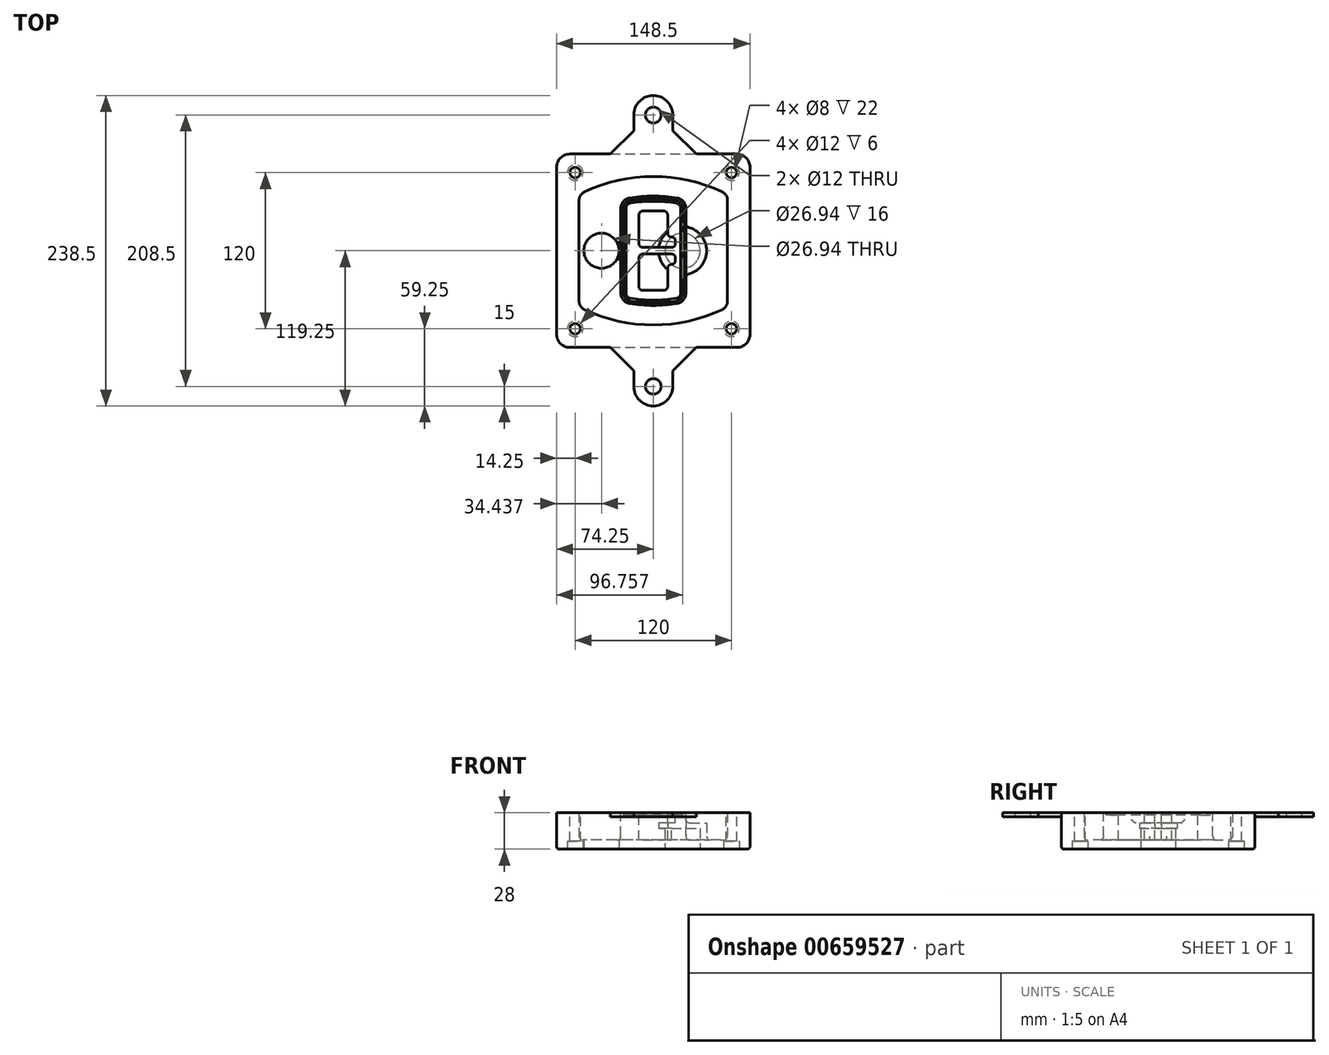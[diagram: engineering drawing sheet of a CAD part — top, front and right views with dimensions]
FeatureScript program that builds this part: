
annotation { "Feature Type Name" : "Feature", "Feature Type Description" : "" }
export const myFeature = defineFeature(function(context is Context, id is Id, definition is map)
    precondition{}
    {
        {
            var Q0;
            Q0=qCreatedBy(makeId("Top.planeOp"),FACE);
            var sketch = newSketch(context, id + "F0", { "sketchPlane" : qUnion([Q0])});
            skPoint(sketch, "E0.rect.middle", {"position": v(0, 0) * mm});
            skLineSegment(sketch, "E1.bottom", {"start": v(-64.25, -74.25) * mm, "end": v(64.25, -74.25) * mm});
            skLineSegment(sketch, "E1.top", {"start": v(-64.25, 74.25) * mm, "end": v(64.25, 74.25) * mm});
            skLineSegment(sketch, "E1.left", {"start": v(-74.25, -64.25) * mm, "end": v(-74.25, 64.25) * mm});
            skLineSegment(sketch, "E1.right", {"start": v(74.25, -64.25) * mm, "end": v(74.25, 64.25) * mm});
            skLineSegment(sketch, "E2", {"start": v(-74.25, 74.25) * mm, "end": v(74.25, -74.25) * mm, "construction": true});
            skLineSegment(sketch, "E3", {"start": v(74.25, 74.25) * mm, "end": v(-74.25, -74.25) * mm, "construction": true});
            skCircle(sketch, "E4", {"center": v(-60, 60) * mm, "radius": 4 * mm});
            skCircle(sketch, "E5", {"center": v(60, 60) * mm, "radius": 4 * mm});
            skCircle(sketch, "E6", {"center": v(60, -60) * mm, "radius": 4 * mm});
            skCircle(sketch, "E7", {"center": v(-60, -60) * mm, "radius": 4 * mm});
            skLineSegment(sketch, "E8", {"start": v(-60, 60) * mm, "end": v(60, 60) * mm, "construction": true});
            skLineSegment(sketch, "E9", {"start": v(60, 60) * mm, "end": v(60, -60) * mm, "construction": true});
            skLineSegment(sketch, "E10", {"start": v(60, -60) * mm, "end": v(-60, -60) * mm, "construction": true});
            skLineSegment(sketch, "E11", {"start": v(-60, -60) * mm, "end": v(-60, 60) * mm, "construction": true});
            skLineSegment(sketch, "E12", {"start": v(-60, 38.83) * mm, "end": v(-60, -38.83) * mm});
            skLineSegment(sketch, "E13", {"start": v(60, 38.83) * mm, "end": v(60, -38.83) * mm});
            skArc(sketch, "E14", {"start": v(54.26, 47.88) * mm, "mid": v(0, 60) * mm, "end": v(-54.26, 47.88) * mm});
            skArc(sketch, "E15", {"start": v(-54.26, -47.88) * mm, "mid": v(0, -60) * mm, "end": v(54.26, -47.88) * mm});
            skLineSegment(sketch, "E16", {"start": v(-60, 0) * mm, "end": v(60, 0) * mm, "construction": true});
            skPoint(sketch, "E17.visualSharp", {"position": v(-60, -45) * mm});
            skArc(sketch, "E17.filletArc", {"start": v(-60, -38.83) * mm, "mid": v(-58.44, -44.2) * mm, "end": v(-54.26, -47.88) * mm});
            skPoint(sketch, "E18.visualSharp", {"position": v(-60, 45) * mm});
            skArc(sketch, "E18.filletArc", {"start": v(-54.26, 47.88) * mm, "mid": v(-58.44, 44.2) * mm, "end": v(-60, 38.83) * mm});
            skPoint(sketch, "E19.visualSharp", {"position": v(60, 45) * mm});
            skArc(sketch, "E19.filletArc", {"start": v(60, 38.83) * mm, "mid": v(58.44, 44.2) * mm, "end": v(54.26, 47.88) * mm});
            skPoint(sketch, "E20.visualSharp", {"position": v(60, -45) * mm});
            skArc(sketch, "E20.filletArc", {"start": v(54.26, -47.88) * mm, "mid": v(58.44, -44.2) * mm, "end": v(60, -38.83) * mm});
            skPoint(sketch, "E21.visualSharp", {"position": v(-74.25, 74.25) * mm});
            skArc(sketch, "E21.filletArc", {"start": v(-64.25, 74.25) * mm, "mid": v(-71.32, 71.32) * mm, "end": v(-74.25, 64.25) * mm});
            skPoint(sketch, "E22.visualSharp", {"position": v(74.25, 74.25) * mm});
            skArc(sketch, "E22.filletArc", {"start": v(74.25, 64.25) * mm, "mid": v(71.32, 71.32) * mm, "end": v(64.25, 74.25) * mm});
            skPoint(sketch, "E23.visualSharp", {"position": v(74.25, -74.25) * mm});
            skArc(sketch, "E23.filletArc", {"start": v(64.25, -74.25) * mm, "mid": v(71.32, -71.32) * mm, "end": v(74.25, -64.25) * mm});
            skPoint(sketch, "E24.visualSharp", {"position": v(-74.25, -74.25) * mm});
            skArc(sketch, "E24.filletArc", {"start": v(-74.25, -64.25) * mm, "mid": v(-71.32, -71.32) * mm, "end": v(-64.25, -74.25) * mm});
            skArc(sketch, "E25.0", {"start": v(57, 38.83) * mm, "mid": v(55.9, 42.58) * mm, "end": v(52.98, 45.17) * mm});
            skLineSegment(sketch, "E25.1", {"start": v(57, 38.83) * mm, "end": v(57, -38.83) * mm});
            skArc(sketch, "E25.2", {"start": v(52.98, -45.17) * mm, "mid": v(55.9, -42.58) * mm, "end": v(57, -38.83) * mm});
            skArc(sketch, "E25.3", {"start": v(-52.98, -45.17) * mm, "mid": v(0, -57) * mm, "end": v(52.98, -45.17) * mm});
            skArc(sketch, "E25.4", {"start": v(-57, -38.83) * mm, "mid": v(-55.9, -42.58) * mm, "end": v(-52.98, -45.17) * mm});
            skArc(sketch, "E25.5", {"start": v(52.98, 45.17) * mm, "mid": v(0, 57) * mm, "end": v(-52.98, 45.17) * mm});
            skLineSegment(sketch, "E25.6", {"start": v(-57, 38.83) * mm, "end": v(-57, -38.83) * mm});
            skArc(sketch, "E25.7", {"start": v(-52.98, 45.17) * mm, "mid": v(-55.9, 42.58) * mm, "end": v(-57, 38.83) * mm});
            skArc(sketch, "E26.0", {"start": v(-55.96, 51.5) * mm, "mid": v(-61.82, 46.33) * mm, "end": v(-64, 38.83) * mm});
            skArc(sketch, "E26.1", {"start": v(55.96, 51.5) * mm, "mid": v(0, 64) * mm, "end": v(-55.96, 51.5) * mm});
            skArc(sketch, "E26.2", {"start": v(64, 38.83) * mm, "mid": v(61.82, 46.33) * mm, "end": v(55.96, 51.5) * mm});
            skLineSegment(sketch, "E26.3", {"start": v(64, 38.83) * mm, "end": v(64, -38.83) * mm});
            skArc(sketch, "E26.4", {"start": v(55.96, -51.5) * mm, "mid": v(61.82, -46.33) * mm, "end": v(64, -38.83) * mm});
            skLineSegment(sketch, "E26.5", {"start": v(-64, 38.83) * mm, "end": v(-64, -38.83) * mm});
            skArc(sketch, "E26.6", {"start": v(-55.96, -51.5) * mm, "mid": v(0, -64) * mm, "end": v(55.96, -51.5) * mm});
            skArc(sketch, "E26.7", {"start": v(-64, -38.83) * mm, "mid": v(-61.82, -46.33) * mm, "end": v(-55.96, -51.5) * mm});
            skSolve(sketch);
        }
        {
            var Q0;
            Q0=makeQuery(id+"F0.imprint","IMPRINT",FACE,{"disambiguationData":[TD([[makeQuery(id+"F0.imprint","IMPRINT",EDGE,{"derivedFrom":sQuery(id+"F0.wireOp",EDGE,"E1.bottom")}),1.0]])]});
            var Q1;
            Q1=makeQuery(id+"F0.imprint","IMPRINT",FACE,{"disambiguationData":[TD([[makeQuery(id+"F0.imprint","IMPRINT",EDGE,{"derivedFrom":sQuery(id+"F0.wireOp",EDGE,"E12")}),1.0]])]});
            var Q2;
            Q2=makeQuery(id+"F0.imprint","IMPRINT",FACE,{"disambiguationData":[TD([[makeQuery(id+"F0.imprint","IMPRINT",EDGE,{"derivedFrom":sQuery(id+"F0.wireOp",EDGE,"E25.0")}),1.0]])]});
            var Q3;
            Q3=makeQuery(id+"F0.imprint","IMPRINT",FACE,{"disambiguationData":[TD([[makeQuery(id+"F0.imprint","IMPRINT",EDGE,{"derivedFrom":sQuery(id+"F0.wireOp",EDGE,"E12")}),-1.0]])]});
            extrude(context, id + "F1", {"entities" : qUnion([Q0, Q1, Q2, Q3]), "oppositeDirection" : true, "depth" : 25 * mm});
        }
        {
            var Q0;
            Q0=makeQuery(id+"F0.imprint","IMPRINT",FACE,{"disambiguationData":[TD([[makeQuery(id+"F0.imprint","IMPRINT",EDGE,{"derivedFrom":sQuery(id+"F0.wireOp",EDGE,"E12")}),1.0]])]});
            extrude(context, id + "F2", {"entities" : qUnion([Q0]), "operationType" : NewBodyOperationType.ADD, "depth" : 3 * mm});
        }
        {
            var Q0;
            Q0=makeQuery(id+"F0.imprint","IMPRINT",FACE,{"disambiguationData":[TD([[makeQuery(id+"F0.imprint","IMPRINT",EDGE,{"derivedFrom":sQuery(id+"F0.wireOp",EDGE,"E25.0")}),1.0]])]});
            extrude(context, id + "F3", {"entities" : qUnion([Q0]), "operationType" : NewBodyOperationType.REMOVE, "oppositeDirection" : true, "depth" : 18 * mm});
        }
        {
            var Q0;
            Q0=makeQuery(id+"F2.opExtrude","CAP_FACE",FACE,{"disambiguationData":[OSD([sQuery(id+"F0.wireOp",EDGE,"E12"),sQuery(id+"F0.wireOp",EDGE,"E13"),sQuery(id+"F0.wireOp",EDGE,"E14"),sQuery(id+"F0.wireOp",EDGE,"E15"),sQuery(id+"F0.wireOp",EDGE,"E17.filletArc"),sQuery(id+"F0.wireOp",EDGE,"E18.filletArc"),sQuery(id+"F0.wireOp",EDGE,"E19.filletArc"),sQuery(id+"F0.wireOp",EDGE,"E20.filletArc"),sQuery(id+"F0.wireOp",EDGE,"E25.0"),sQuery(id+"F0.wireOp",EDGE,"E25.1"),sQuery(id+"F0.wireOp",EDGE,"E25.2"),sQuery(id+"F0.wireOp",EDGE,"E25.3"),sQuery(id+"F0.wireOp",EDGE,"E25.4"),sQuery(id+"F0.wireOp",EDGE,"E25.5"),sQuery(id+"F0.wireOp",EDGE,"E25.6"),sQuery(id+"F0.wireOp",EDGE,"E25.7")])],"isStart":false});
            var sketch = newSketch(context, id + "F4", { "sketchPlane" : qUnion([Q0])});
            skArc(sketch, "E27.0", {"start": v(-18.34, -40.45) * mm, "mid": v(0, -42) * mm, "end": v(18.34, -40.45) * mm});
            skArc(sketch, "E28.0", {"start": v(18.34, 40.45) * mm, "mid": v(0, 42) * mm, "end": v(-18.34, 40.45) * mm});
            skLineSegment(sketch, "E29", {"start": v(-25, 32.57) * mm, "end": v(-25, -32.57) * mm});
            skLineSegment(sketch, "E30", {"start": v(25, 32.57) * mm, "end": v(25, -32.57) * mm});
            skLineSegment(sketch, "E31", {"start": v(-25, 39.1) * mm, "end": v(25, 39.1) * mm, "construction": true});
            skLineSegment(sketch, "E32", {"start": v(-25, -39.1) * mm, "end": v(25, -39.1) * mm, "construction": true});
            skPoint(sketch, "E33.visualSharp", {"position": v(-25, 39.1) * mm});
            skArc(sketch, "E33.filletArc", {"start": v(-18.34, 40.45) * mm, "mid": v(-23.11, 37.73) * mm, "end": v(-25, 32.57) * mm});
            skPoint(sketch, "E34.visualSharp", {"position": v(25, 39.1) * mm});
            skArc(sketch, "E34.filletArc", {"start": v(25, 32.57) * mm, "mid": v(23.11, 37.73) * mm, "end": v(18.34, 40.45) * mm});
            skPoint(sketch, "E35.visualSharp", {"position": v(25, -39.1) * mm});
            skArc(sketch, "E35.filletArc", {"start": v(18.34, -40.45) * mm, "mid": v(23.11, -37.73) * mm, "end": v(25, -32.57) * mm});
            skPoint(sketch, "E36.visualSharp", {"position": v(-25, -39.1) * mm});
            skArc(sketch, "E36.filletArc", {"start": v(-25, -32.57) * mm, "mid": v(-23.11, -37.73) * mm, "end": v(-18.34, -40.45) * mm});
            skArc(sketch, "E37.0", {"start": v(52.98, 45.17) * mm, "mid": v(0, 57) * mm, "end": v(-52.98, 45.17) * mm});
            skArc(sketch, "E37.1", {"start": v(-52.98, 45.17) * mm, "mid": v(-55.9, 42.58) * mm, "end": v(-57, 38.83) * mm});
            skLineSegment(sketch, "E37.2", {"start": v(-57, 38.83) * mm, "end": v(-57, -38.83) * mm});
            skArc(sketch, "E37.3", {"start": v(-57, -38.83) * mm, "mid": v(-55.9, -42.58) * mm, "end": v(-52.98, -45.17) * mm});
            skArc(sketch, "E37.4", {"start": v(-52.98, -45.17) * mm, "mid": v(0, -57) * mm, "end": v(52.98, -45.17) * mm});
            skArc(sketch, "E37.5", {"start": v(52.98, -45.17) * mm, "mid": v(55.9, -42.58) * mm, "end": v(57, -38.83) * mm});
            skLineSegment(sketch, "E37.6", {"start": v(57, 38.83) * mm, "end": v(57, -38.83) * mm});
            skArc(sketch, "E37.7", {"start": v(57, 38.83) * mm, "mid": v(55.9, 42.58) * mm, "end": v(52.98, 45.17) * mm});
            skLineSegment(sketch, "E38.0", {"start": v(23, 32.57) * mm, "end": v(23, -32.57) * mm});
            skArc(sketch, "E38.1", {"start": v(18, -38.48) * mm, "mid": v(21.58, -36.44) * mm, "end": v(23, -32.57) * mm});
            skArc(sketch, "E38.2", {"start": v(-18, -38.48) * mm, "mid": v(0, -40) * mm, "end": v(18, -38.48) * mm});
            skArc(sketch, "E38.3", {"start": v(-23, -32.57) * mm, "mid": v(-21.58, -36.44) * mm, "end": v(-18, -38.48) * mm});
            skLineSegment(sketch, "E38.4", {"start": v(-23, 32.57) * mm, "end": v(-23, -32.57) * mm});
            skArc(sketch, "E38.5", {"start": v(23, 32.57) * mm, "mid": v(21.58, 36.44) * mm, "end": v(18, 38.48) * mm});
            skArc(sketch, "E38.6", {"start": v(-18, 38.48) * mm, "mid": v(-21.58, 36.44) * mm, "end": v(-23, 32.57) * mm});
            skArc(sketch, "E38.7", {"start": v(18, 38.48) * mm, "mid": v(0, 40) * mm, "end": v(-18, 38.48) * mm});
            skArc(sketch, "E39.0", {"start": v(21, 32.57) * mm, "mid": v(20.06, 35.15) * mm, "end": v(17.67, 36.5) * mm});
            skLineSegment(sketch, "E39.1", {"start": v(21, 32.57) * mm, "end": v(21, -32.57) * mm});
            skArc(sketch, "E39.2", {"start": v(17.67, -36.5) * mm, "mid": v(20.06, -35.15) * mm, "end": v(21, -32.57) * mm});
            skArc(sketch, "E39.3", {"start": v(-17.67, -36.5) * mm, "mid": v(0, -38) * mm, "end": v(17.67, -36.5) * mm});
            skArc(sketch, "E39.4", {"start": v(-21, -32.57) * mm, "mid": v(-20.06, -35.15) * mm, "end": v(-17.67, -36.5) * mm});
            skArc(sketch, "E39.5", {"start": v(17.67, 36.5) * mm, "mid": v(0, 38) * mm, "end": v(-17.67, 36.5) * mm});
            skLineSegment(sketch, "E39.6", {"start": v(-21, 32.57) * mm, "end": v(-21, -32.57) * mm});
            skArc(sketch, "E39.7", {"start": v(-17.67, 36.5) * mm, "mid": v(-20.06, 35.15) * mm, "end": v(-21, 32.57) * mm});
            skLineSegment(sketch, "E40", {"start": v(-25, 0) * mm, "end": v(25, 0) * mm, "construction": true});
            skLineSegment(sketch, "E41", {"start": v(-11, 5.5) * mm, "end": v(-11, 27.5) * mm});
            skLineSegment(sketch, "E42", {"start": v(-8, 30.5) * mm, "end": v(8, 30.5) * mm});
            skLineSegment(sketch, "E43", {"start": v(11, 27.5) * mm, "end": v(11, 13.5) * mm});
            skLineSegment(sketch, "E44", {"start": v(14, 10.5) * mm, "end": v(14, 10.5) * mm});
            skLineSegment(sketch, "E45", {"start": v(17, 7.5) * mm, "end": v(17, 5.5) * mm});
            skLineSegment(sketch, "E46", {"start": v(14, 2.5) * mm, "end": v(-8, 2.5) * mm});
            skPoint(sketch, "E47.visualSharp", {"position": v(-11, 30.5) * mm});
            skArc(sketch, "E47.filletArc", {"start": v(-8, 30.5) * mm, "mid": v(-10.12, 29.62) * mm, "end": v(-11, 27.5) * mm});
            skPoint(sketch, "E48.visualSharp", {"position": v(11, 30.5) * mm});
            skArc(sketch, "E48.filletArc", {"start": v(11, 27.5) * mm, "mid": v(10.12, 29.62) * mm, "end": v(8, 30.5) * mm});
            skPoint(sketch, "E49.visualSharp", {"position": v(11, 10.5) * mm});
            skArc(sketch, "E49.filletArc", {"start": v(11, 13.5) * mm, "mid": v(11.88, 11.38) * mm, "end": v(14, 10.5) * mm});
            skPoint(sketch, "E50.visualSharp", {"position": v(17, 10.5) * mm});
            skArc(sketch, "E50.filletArc", {"start": v(17, 7.5) * mm, "mid": v(16.12, 9.62) * mm, "end": v(14, 10.5) * mm});
            skPoint(sketch, "E51.visualSharp", {"position": v(17, 2.5) * mm});
            skArc(sketch, "E51.filletArc", {"start": v(14, 2.5) * mm, "mid": v(16.12, 3.38) * mm, "end": v(17, 5.5) * mm});
            skPoint(sketch, "E52.visualSharp", {"position": v(-11, 2.5) * mm});
            skArc(sketch, "E52.filletArc", {"start": v(-11, 5.5) * mm, "mid": v(-10.12, 3.38) * mm, "end": v(-8, 2.5) * mm});
            skLineSegment(sketch, "E53.0.MirrorCS", {"start": v(14, -2.5) * mm, "end": v(-8, -2.5) * mm});
            skArc(sketch, "E54.0.MirrorCS", {"start": v(-11, -5.5) * mm, "mid": v(-10.12, -3.38) * mm, "end": v(-8, -2.5) * mm});
            skLineSegment(sketch, "E55.0.MirrorCS", {"start": v(-11, -5.5) * mm, "end": v(-11, -27.5) * mm});
            skArc(sketch, "E56.0.MirrorCS", {"start": v(-8, -30.5) * mm, "mid": v(-10.12, -29.62) * mm, "end": v(-11, -27.5) * mm});
            skLineSegment(sketch, "E57.0.MirrorCS", {"start": v(-8, -30.5) * mm, "end": v(8, -30.5) * mm});
            skArc(sketch, "E58.0.MirrorCS", {"start": v(11, -27.5) * mm, "mid": v(10.12, -29.62) * mm, "end": v(8, -30.5) * mm});
            skLineSegment(sketch, "E59.0.MirrorCS", {"start": v(11, -27.5) * mm, "end": v(11, -13.5) * mm});
            skArc(sketch, "E60.0.MirrorCS", {"start": v(11, -13.5) * mm, "mid": v(11.88, -11.38) * mm, "end": v(14, -10.5) * mm});
            skArc(sketch, "E61.0.MirrorCS", {"start": v(17, -7.5) * mm, "mid": v(16.12, -9.62) * mm, "end": v(14, -10.5) * mm});
            skLineSegment(sketch, "E62.0.MirrorCS", {"start": v(17, -7.5) * mm, "end": v(17, -5.5) * mm});
            skArc(sketch, "E63.0.MirrorCS", {"start": v(14, -2.5) * mm, "mid": v(16.12, -3.38) * mm, "end": v(17, -5.5) * mm});
            skSolve(sketch);
        }
        {
            var Q0;
            Q0=makeQuery(id+"F4.imprint","IMPRINT",FACE,{"disambiguationData":[TD([[makeQuery(id+"F4.imprint","IMPRINT",EDGE,{"derivedFrom":sQuery(id+"F4.wireOp",EDGE,"E27.0")}),1.0]])]});
            var Q1;
            Q1=makeQuery(id+"F4.imprint","IMPRINT",FACE,{"disambiguationData":[TD([[makeQuery(id+"F4.imprint","IMPRINT",EDGE,{"derivedFrom":sQuery(id+"F4.wireOp",EDGE,"E38.0")}),-1.0]])]});
            var Q2;
            Q2=makeQuery(id+"F4.imprint","IMPRINT",FACE,{"disambiguationData":[TD([[makeQuery(id+"F4.imprint","IMPRINT",EDGE,{"derivedFrom":sQuery(id+"F4.wireOp",EDGE,"E39.0")}),1.0]])]});
            extrude(context, id + "F5", {"entities" : qUnion([Q0, Q1, Q2]), "operationType" : NewBodyOperationType.ADD, "endBound" : BoundingType.UP_TO_NEXT, "oppositeDirection" : true, "depth" : 25 * mm});
        }
        {
            var Q0;
            Q0=makeQuery(id+"F4.imprint","IMPRINT",FACE,{"disambiguationData":[TD([[makeQuery(id+"F4.imprint","IMPRINT",EDGE,{"derivedFrom":sQuery(id+"F4.wireOp",EDGE,"E38.0")}),-1.0]])]});
            extrude(context, id + "F6", {"entities" : qUnion([Q0]), "operationType" : NewBodyOperationType.REMOVE, "oppositeDirection" : true, "depth" : 2 * mm});
        }
        {
            var Q0;
            Q0=makeQuery(id+"F1.opExtrude","CAP_FACE",FACE,{"disambiguationData":[OSD([sQuery(id+"F0.wireOp",EDGE,"E1.bottom"),sQuery(id+"F0.wireOp",EDGE,"E1.top"),sQuery(id+"F0.wireOp",EDGE,"E1.left"),sQuery(id+"F0.wireOp",EDGE,"E1.right"),sQuery(id+"F0.wireOp",EDGE,"E4"),sQuery(id+"F0.wireOp",EDGE,"E5"),sQuery(id+"F0.wireOp",EDGE,"E6"),sQuery(id+"F0.wireOp",EDGE,"E7"),sQuery(id+"F0.wireOp",EDGE,"E21.filletArc"),sQuery(id+"F0.wireOp",EDGE,"E22.filletArc"),sQuery(id+"F0.wireOp",EDGE,"E23.filletArc"),sQuery(id+"F0.wireOp",EDGE,"E24.filletArc")])],"isStart":false});
            var sketch = newSketch(context, id + "F7", { "sketchPlane" : qUnion([Q0])});
            skCircle(sketch, "E64", {"center": v(22.5, 0) * mm, "radius": 13.47 * mm});
            skCircle(sketch, "E65", {"center": v(-39.81, 0) * mm, "radius": 13.47 * mm});
            skLineSegment(sketch, "E66", {"start": v(74.25, 0) * mm, "end": v(-74.25, 0) * mm});
            skCircle(sketch, "E67", {"center": v(22.5, 0) * mm, "radius": 18.47 * mm});
            skCircle(sketch, "E68", {"center": v(60, -60) * mm, "radius": 6 * mm});
            skCircle(sketch, "E69", {"center": v(-60, -60) * mm, "radius": 6 * mm});
            skCircle(sketch, "E70", {"center": v(-60, 60) * mm, "radius": 6 * mm});
            skCircle(sketch, "E71", {"center": v(60, 60) * mm, "radius": 6 * mm});
            skSolve(sketch);
        }
        {
            var Q0;
            {var subQ1=sQuery(id+"F7.wireOp",EDGE,"E66");var subQ4=sQuery(id+"F7.wireOp",EDGE,"E64");var subQ6=makeQuery(id+"F7.imprint","INTERSECT",VERTEX,{"disambiguationData":[OD(0.0)],"derivedFrom":[subQ4,subQ1]});Q0=makeQuery(id+"F7.imprint","IMPRINT",FACE,{"disambiguationData":[TD([[makeQuery(id+"F7.imprint","IMPRINT",EDGE,{"disambiguationData":[TD([[subQ6,-1.0]])],"derivedFrom":subQ4}),-1.0]])]});}
            var Q1;
            {var subQ0=sQuery(id+"F7.wireOp",EDGE,"E66");var subQ1=sQuery(id+"F7.wireOp",EDGE,"E64");var subQ3=makeQuery(id+"F7.imprint","INTERSECT",VERTEX,{"disambiguationData":[OD(0.0)],"derivedFrom":[subQ1,subQ0]});Q1=makeQuery(id+"F7.imprint","IMPRINT",FACE,{"disambiguationData":[TD([[makeQuery(id+"F7.imprint","IMPRINT",EDGE,{"disambiguationData":[TD([[subQ3,-1.0]])],"derivedFrom":subQ1}),1.0]])]});}
            var Q2;
            {var subQ0=sQuery(id+"F7.wireOp",EDGE,"E66");var subQ1=sQuery(id+"F7.wireOp",EDGE,"E64");var subQ3=makeQuery(id+"F7.imprint","INTERSECT",VERTEX,{"disambiguationData":[OD(0.0)],"derivedFrom":[subQ1,subQ0]});Q2=makeQuery(id+"F7.imprint","IMPRINT",FACE,{"disambiguationData":[TD([[makeQuery(id+"F7.imprint","IMPRINT",EDGE,{"disambiguationData":[TD([[subQ3,1.0]])],"derivedFrom":subQ1}),1.0]])]});}
            var Q3;
            {var subQ1=sQuery(id+"F7.wireOp",EDGE,"E66");var subQ4=sQuery(id+"F7.wireOp",EDGE,"E64");var subQ6=makeQuery(id+"F7.imprint","INTERSECT",VERTEX,{"disambiguationData":[OD(0.0)],"derivedFrom":[subQ4,subQ1]});Q3=makeQuery(id+"F7.imprint","IMPRINT",FACE,{"disambiguationData":[TD([[makeQuery(id+"F7.imprint","IMPRINT",EDGE,{"disambiguationData":[TD([[subQ6,1.0]])],"derivedFrom":subQ4}),-1.0]])]});}
            extrude(context, id + "F8", {"entities" : qUnion([Q0, Q1, Q2, Q3]), "operationType" : NewBodyOperationType.ADD, "oppositeDirection" : true, "depth" : 20 * mm});
        }
        {
            var Q0;
            {var subQ0=sQuery(id+"F7.wireOp",EDGE,"E66");var subQ1=sQuery(id+"F7.wireOp",EDGE,"E64");var subQ3=makeQuery(id+"F7.imprint","INTERSECT",VERTEX,{"disambiguationData":[OD(0.0)],"derivedFrom":[subQ1,subQ0]});Q0=makeQuery(id+"F7.imprint","IMPRINT",FACE,{"disambiguationData":[TD([[makeQuery(id+"F7.imprint","IMPRINT",EDGE,{"disambiguationData":[TD([[subQ3,-1.0]])],"derivedFrom":subQ1}),1.0]])]});}
            var Q1;
            {var subQ0=sQuery(id+"F7.wireOp",EDGE,"E66");var subQ1=sQuery(id+"F7.wireOp",EDGE,"E64");var subQ3=makeQuery(id+"F7.imprint","INTERSECT",VERTEX,{"disambiguationData":[OD(0.0)],"derivedFrom":[subQ1,subQ0]});Q1=makeQuery(id+"F7.imprint","IMPRINT",FACE,{"disambiguationData":[TD([[makeQuery(id+"F7.imprint","IMPRINT",EDGE,{"disambiguationData":[TD([[subQ3,1.0]])],"derivedFrom":subQ1}),1.0]])]});}
            extrude(context, id + "F9", {"entities" : qUnion([Q0, Q1]), "operationType" : NewBodyOperationType.REMOVE, "oppositeDirection" : true, "depth" : 16 * mm});
        }
        {
            var Q0;
            {var subQ0=sQuery(id+"F7.wireOp",EDGE,"E66");var subQ1=sQuery(id+"F7.wireOp",EDGE,"E65");var subQ3=makeQuery(id+"F7.imprint","INTERSECT",VERTEX,{"disambiguationData":[OD(0.0)],"derivedFrom":[subQ1,subQ0]});Q0=makeQuery(id+"F7.imprint","IMPRINT",FACE,{"disambiguationData":[TD([[makeQuery(id+"F7.imprint","IMPRINT",EDGE,{"disambiguationData":[TD([[subQ3,-1.0]])],"derivedFrom":subQ1}),1.0]])]});}
            var Q1;
            {var subQ0=sQuery(id+"F7.wireOp",EDGE,"E66");var subQ1=sQuery(id+"F7.wireOp",EDGE,"E65");var subQ3=makeQuery(id+"F7.imprint","INTERSECT",VERTEX,{"disambiguationData":[OD(0.0)],"derivedFrom":[subQ1,subQ0]});Q1=makeQuery(id+"F7.imprint","IMPRINT",FACE,{"disambiguationData":[TD([[makeQuery(id+"F7.imprint","IMPRINT",EDGE,{"disambiguationData":[TD([[subQ3,1.0]])],"derivedFrom":subQ1}),1.0]])]});}
            extrude(context, id + "F10", {"entities" : qUnion([Q0, Q1]), "operationType" : NewBodyOperationType.REMOVE, "oppositeDirection" : true, "depth" : 25 * mm});
        }
        {
            var Q0;
            Q0=makeQuery(id+"F7.imprint","IMPRINT",FACE,{"disambiguationData":[TD([[makeQuery(id+"F7.imprint","IMPRINT",EDGE,{"derivedFrom":sQuery(id+"F7.wireOp",EDGE,"E68")}),1.0]])]});
            var Q1;
            Q1=makeQuery(id+"F7.imprint","IMPRINT",FACE,{"disambiguationData":[TD([[makeQuery(id+"F7.imprint","IMPRINT",EDGE,{"derivedFrom":makeQuery(id+"F1.opExtrude","CAP_EDGE",EDGE,{"disambiguationData":[OSD([sQuery(id+"F0.wireOp",EDGE,"E5")])],"isStart":false})}),-1.0]])]});
            var Q2;
            Q2=makeQuery(id+"F7.imprint","IMPRINT",FACE,{"disambiguationData":[TD([[makeQuery(id+"F7.imprint","IMPRINT",EDGE,{"derivedFrom":sQuery(id+"F7.wireOp",EDGE,"E69")}),1.0]])]});
            var Q3;
            Q3=makeQuery(id+"F7.imprint","IMPRINT",FACE,{"disambiguationData":[TD([[makeQuery(id+"F7.imprint","IMPRINT",EDGE,{"derivedFrom":makeQuery(id+"F1.opExtrude","CAP_EDGE",EDGE,{"disambiguationData":[OSD([sQuery(id+"F0.wireOp",EDGE,"E4")])],"isStart":false})}),-1.0]])]});
            var Q4;
            Q4=makeQuery(id+"F7.imprint","IMPRINT",FACE,{"disambiguationData":[TD([[makeQuery(id+"F7.imprint","IMPRINT",EDGE,{"derivedFrom":sQuery(id+"F7.wireOp",EDGE,"E70")}),1.0]])]});
            var Q5;
            Q5=makeQuery(id+"F7.imprint","IMPRINT",FACE,{"disambiguationData":[TD([[makeQuery(id+"F7.imprint","IMPRINT",EDGE,{"derivedFrom":makeQuery(id+"F1.opExtrude","CAP_EDGE",EDGE,{"disambiguationData":[OSD([sQuery(id+"F0.wireOp",EDGE,"E7")])],"isStart":false})}),-1.0]])]});
            var Q6;
            Q6=makeQuery(id+"F7.imprint","IMPRINT",FACE,{"disambiguationData":[TD([[makeQuery(id+"F7.imprint","IMPRINT",EDGE,{"derivedFrom":sQuery(id+"F7.wireOp",EDGE,"E71")}),1.0]])]});
            var Q7;
            Q7=makeQuery(id+"F7.imprint","IMPRINT",FACE,{"disambiguationData":[TD([[makeQuery(id+"F7.imprint","IMPRINT",EDGE,{"derivedFrom":makeQuery(id+"F1.opExtrude","CAP_EDGE",EDGE,{"disambiguationData":[OSD([sQuery(id+"F0.wireOp",EDGE,"E6")])],"isStart":false})}),-1.0]])]});
            extrude(context, id + "F11", {"entities" : qUnion([Q0, Q1, Q2, Q3, Q4, Q5, Q6, Q7]), "operationType" : NewBodyOperationType.REMOVE, "oppositeDirection" : true, "depth" : 6 * mm});
        }
        {
            var Q0;
            Q0=makeQuery(id+"F9.boolean.opBoolean","COPY",FACE,{"derivedFrom":makeQuery(id+"F9.opExtrude","CAP_FACE",FACE,{"disambiguationData":[OSD([sQuery(id+"F7.wireOp",EDGE,"E64")])],"isStart":false})});
            var sketch = newSketch(context, id + "F12", { "sketchPlane" : qUnion([Q0])});
            skArc(sketch, "E72.0", {"start": v(11, 14.45) * mm, "mid": v(6.45, 9.13) * mm, "end": v(4.2, 2.5) * mm});
            skArc(sketch, "E72.1", {"start": v(4.2, -2.5) * mm, "mid": v(6.45, -9.13) * mm, "end": v(11, -14.45) * mm});
            skLineSegment(sketch, "E73", {"start": v(4.2, -2.5) * mm, "end": v(14, -2.5) * mm});
            skLineSegment(sketch, "E74.0", {"start": v(14, 2.5) * mm, "end": v(4.2, 2.5) * mm});
            skArc(sketch, "E74.1", {"start": v(14, 2.5) * mm, "mid": v(16.12, 3.38) * mm, "end": v(17, 5.5) * mm});
            skLineSegment(sketch, "E74.2", {"start": v(17, 7.5) * mm, "end": v(17, 5.5) * mm});
            skArc(sketch, "E74.3", {"start": v(17, 7.5) * mm, "mid": v(16.12, 9.62) * mm, "end": v(14, 10.5) * mm});
            skArc(sketch, "E74.4", {"start": v(11, 13.5) * mm, "mid": v(11.88, 11.38) * mm, "end": v(14, 10.5) * mm});
            skLineSegment(sketch, "E74.5", {"start": v(11, 14.45) * mm, "end": v(11, 13.5) * mm});
            skLineSegment(sketch, "E74.7", {"start": v(14, -2.5) * mm, "end": v(4.2, -2.5) * mm});
            skArc(sketch, "E74.8", {"start": v(14, -2.5) * mm, "mid": v(16.12, -3.38) * mm, "end": v(17, -5.5) * mm});
            skLineSegment(sketch, "E74.9", {"start": v(17, -7.5) * mm, "end": v(17, -5.5) * mm});
            skArc(sketch, "E74.10", {"start": v(17, -7.5) * mm, "mid": v(16.12, -9.62) * mm, "end": v(14, -10.5) * mm});
            skArc(sketch, "E74.11", {"start": v(11, -13.5) * mm, "mid": v(11.88, -11.38) * mm, "end": v(14, -10.5) * mm});
            skLineSegment(sketch, "E74.12", {"start": v(11, -14.45) * mm, "end": v(11, -13.5) * mm});
            skPoint(sketch, "E75.orphan", {"position": v(11, -27.5) * mm});
            skPoint(sketch, "E76.orphan", {"position": v(-8, -2.5) * mm});
            skPoint(sketch, "E77.orphan", {"position": v(-8, 2.5) * mm});
            skPoint(sketch, "E78.orphan", {"position": v(11, 27.5) * mm});
            skSolve(sketch);
        }
        {
            var Q0;
            {var subQ7=sQuery(id+"F12.wireOp",EDGE,"E72.0");var subQ14=sQuery(id+"F12.wireOp",EDGE,"E72.1");var subQ16=sQuery(id+"F12.wireOp",EDGE,"E74.1");var subQ18=sQuery(id+"F12.wireOp",EDGE,"E74.8");Q0=qUnion([makeQuery(id+"F12.imprint","IMPRINT",FACE,{"disambiguationData":[TD([[makeQuery(id+"F12.imprint","IMPRINT",EDGE,{"derivedFrom":subQ7}),1.0]])]}),makeQuery(id+"F12.imprint","IMPRINT",FACE,{"disambiguationData":[TD([[makeQuery(id+"F12.imprint","IMPRINT",EDGE,{"derivedFrom":subQ14}),1.0]])]}),makeQuery(id+"F12.imprint","IMPRINT",FACE,{"disambiguationData":[TD([[makeQuery(id+"F12.imprint","IMPRINT",EDGE,{"derivedFrom":subQ16}),1.0]])]}),makeQuery(id+"F12.imprint","IMPRINT",FACE,{"disambiguationData":[TD([[makeQuery(id+"F12.imprint","IMPRINT",EDGE,{"derivedFrom":subQ18}),-1.0]])]})]);}
            var Q1;
            Q1=makeQuery(id+"F5.boolean.opBoolean","SPLIT",FACE,{"disambiguationData":[TD([makeQuery(id+"F5.opExtrude","SWEPT_FACE",FACE,{"disambiguationData":[OSD([sQuery(id+"F4.wireOp",EDGE,"E41")])]})])],"derivedFrom":makeQuery(id+"F3.boolean.opBoolean","COPY",FACE,{"derivedFrom":makeQuery(id+"F3.opExtrude","CAP_FACE",FACE,{"disambiguationData":[OSD([sQuery(id+"F0.wireOp",EDGE,"E25.0"),sQuery(id+"F0.wireOp",EDGE,"E25.1"),sQuery(id+"F0.wireOp",EDGE,"E25.2"),sQuery(id+"F0.wireOp",EDGE,"E25.3"),sQuery(id+"F0.wireOp",EDGE,"E25.4"),sQuery(id+"F0.wireOp",EDGE,"E25.5"),sQuery(id+"F0.wireOp",EDGE,"E25.6"),sQuery(id+"F0.wireOp",EDGE,"E25.7")])],"isStart":false})})});
            extrude(context, id + "F13", {"entities" : qUnion([Q0]), "operationType" : NewBodyOperationType.REMOVE, "endBound" : BoundingType.UP_TO_SURFACE, "endBoundEntityFace" : qUnion([Q1]), "depth" : 25 * mm});
        }
        {
            var Q0;
            Q0=makeQuery(id+"F3.boolean.opBoolean","COPY",EDGE,{"derivedFrom":makeQuery(id+"F3.opExtrude","CAP_EDGE",EDGE,{"disambiguationData":[OSD([sQuery(id+"F0.wireOp",EDGE,"E25.6")])],"isStart":false})});
            var Q1;
            Q1=makeQuery(id+"F8.boolean.opBoolean","INTERSECT",EDGE,{"derivedFrom":[makeQuery(id+"F5.opExtrude","SWEPT_FACE",FACE,{"disambiguationData":[OSD([sQuery(id+"F4.wireOp",EDGE,"E30")])]}),makeQuery(id+"F8.opExtrude","CAP_FACE",FACE,{"disambiguationData":[OSD([sQuery(id+"F7.wireOp",EDGE,"E67")])],"isStart":false})]});
            var Q2;
            Q2=makeQuery(id+"F8.boolean.opBoolean","INTERSECT",EDGE,{"disambiguationData":[OD(1.0)],"derivedFrom":[makeQuery(id+"F5.opExtrude","SWEPT_FACE",FACE,{"disambiguationData":[OSD([sQuery(id+"F4.wireOp",EDGE,"E30")])]}),makeQuery(id+"F8.opExtrude","SWEPT_FACE",FACE,{"disambiguationData":[OSD([sQuery(id+"F7.wireOp",EDGE,"E67")])]})]});
            var Q3;
            {var subQ0=sQuery(id+"F4.wireOp",EDGE,"E30");Q3=makeQuery(id+"F8.boolean.opBoolean","SPLIT",EDGE,{"disambiguationData":[TD([makeQuery(id+"F5.opExtrude","SWEPT_FACE",FACE,{"disambiguationData":[OSD([sQuery(id+"F4.wireOp",EDGE,"E35.filletArc")])]})])],"derivedFrom":makeQuery(id+"F5.opExtrude","CAP_EDGE",EDGE,{"disambiguationData":[OSD([subQ0])],"isStart":false})});}
            var Q4;
            {var subQ0=sQuery(id+"F0.wireOp",EDGE,"E25.7");var subQ1=sQuery(id+"F0.wireOp",EDGE,"E25.1");var subQ2=sQuery(id+"F0.wireOp",EDGE,"E25.6");var subQ3=sQuery(id+"F0.wireOp",EDGE,"E25.5");var subQ4=sQuery(id+"F0.wireOp",EDGE,"E25.4");var subQ5=sQuery(id+"F0.wireOp",EDGE,"E25.0");var subQ6=sQuery(id+"F0.wireOp",EDGE,"E25.2");var subQ7=sQuery(id+"F0.wireOp",EDGE,"E25.3");Q4=makeQuery(id+"F8.boolean.opBoolean","INTERSECT",EDGE,{"derivedFrom":[makeQuery(id+"F5.boolean.opBoolean","SPLIT",FACE,{"disambiguationData":[TD([makeQuery(id+"F2.opExtrude","SWEPT_FACE",FACE,{"disambiguationData":[OSD([subQ5])]})])],"derivedFrom":makeQuery(id+"F3.boolean.opBoolean","COPY",FACE,{"derivedFrom":makeQuery(id+"F3.opExtrude","CAP_FACE",FACE,{"disambiguationData":[OSD([subQ5,subQ1,subQ6,subQ7,subQ4,subQ3,subQ2,subQ0])],"isStart":false})})}),makeQuery(id+"F8.opExtrude","SWEPT_FACE",FACE,{"disambiguationData":[OSD([sQuery(id+"F7.wireOp",EDGE,"E67")])]})]});}
            var Q5;
            Q5=makeQuery(id+"F8.boolean.opBoolean","INTERSECT",EDGE,{"disambiguationData":[OD(0.0)],"derivedFrom":[makeQuery(id+"F5.opExtrude","SWEPT_FACE",FACE,{"disambiguationData":[OSD([sQuery(id+"F4.wireOp",EDGE,"E30")])]}),makeQuery(id+"F8.opExtrude","SWEPT_FACE",FACE,{"disambiguationData":[OSD([sQuery(id+"F7.wireOp",EDGE,"E67")])]})]});
            fillet(context, id + "F14", {"entities" : qUnion([Q0, Q1, Q2, Q3, Q4, Q5]), "radius" : 3 * mm, "tangentPropagation" : true, "allowEdgeOverflow" : false});
        }
        {
            var Q0;
            Q0=makeQuery(id+"F1.opExtrude","CAP_EDGE",EDGE,{"disambiguationData":[OSD([sQuery(id+"F0.wireOp",EDGE,"E1.bottom")])],"isStart":false});
            fillet(context, id + "F15", {"entities" : qUnion([Q0]), "radius" : 2 * mm, "tangentPropagation" : true, "allowEdgeOverflow" : false});
        }
        {
            var Q0;
            {var subQ0=sQuery(id+"F0.wireOp",EDGE,"E21.filletArc");var subQ1=sQuery(id+"F0.wireOp",EDGE,"E7");var subQ2=sQuery(id+"F0.wireOp",EDGE,"E6");var subQ3=sQuery(id+"F0.wireOp",EDGE,"E5");var subQ4=sQuery(id+"F0.wireOp",EDGE,"E4");var subQ5=sQuery(id+"F0.wireOp",EDGE,"E22.filletArc");var subQ6=sQuery(id+"F0.wireOp",EDGE,"E1.bottom");var subQ7=sQuery(id+"F0.wireOp",EDGE,"E1.right");var subQ8=sQuery(id+"F0.wireOp",EDGE,"E1.top");var subQ9=sQuery(id+"F0.wireOp",EDGE,"E1.left");var subQ10=sQuery(id+"F0.wireOp",EDGE,"E23.filletArc");var subQ11=sQuery(id+"F0.wireOp",EDGE,"E24.filletArc");Q0=makeQuery(id+"F2.boolean.opBoolean","SPLIT",FACE,{"disambiguationData":[TD([makeQuery(id+"F1.opExtrude","SWEPT_FACE",FACE,{"disambiguationData":[OSD([subQ6])]})])],"derivedFrom":makeQuery(id+"F1.opExtrude","CAP_FACE",FACE,{"disambiguationData":[OSD([subQ6,subQ8,subQ9,subQ7,subQ4,subQ3,subQ2,subQ1,subQ0,subQ5,subQ10,subQ11])],"isStart":true})});}
            var sketch = newSketch(context, id + "F16", { "sketchPlane" : qUnion([Q0])});
            skLineSegment(sketch, "E79", {"start": v(0, 74.25) * mm, "end": v(0, -74.25) * mm, "construction": true});
            skLineSegment(sketch, "E80", {"start": v(-15, 104.25) * mm, "end": v(-15, 92.25) * mm});
            skLineSegment(sketch, "E81", {"start": v(15, 104.25) * mm, "end": v(15, 92.25) * mm});
            skLineSegment(sketch, "E82", {"start": v(-15, 92.25) * mm, "end": v(-33, 74.25) * mm});
            skLineSegment(sketch, "E83", {"start": v(15, 92.25) * mm, "end": v(33, 74.25) * mm});
            skArc(sketch, "E84", {"start": v(15, 104.25) * mm, "mid": v(0, 119.25) * mm, "end": v(-15, 104.25) * mm});
            skCircle(sketch, "E85", {"center": v(0, 104.25) * mm, "radius": 6 * mm});
            skLineSegment(sketch, "E86", {"start": v(-74.25, 0) * mm, "end": v(74.25, 0) * mm, "construction": true});
            skLineSegment(sketch, "E87.MirrorCS", {"start": v(15, -104.25) * mm, "end": v(15, -92.25) * mm});
            skLineSegment(sketch, "E88.MirrorCS", {"start": v(-15, -104.25) * mm, "end": v(-15, -92.25) * mm});
            skLineSegment(sketch, "E89.MirrorCS", {"start": v(15, -92.25) * mm, "end": v(33, -74.25) * mm});
            skLineSegment(sketch, "E90.MirrorCS", {"start": v(-15, -92.25) * mm, "end": v(-33, -74.25) * mm});
            skArc(sketch, "E91.MirrorCS", {"start": v(15, -104.25) * mm, "mid": v(0, -119.25) * mm, "end": v(-15, -104.25) * mm});
            skCircle(sketch, "E92.MirrorC", {"center": v(0, -104.25) * mm, "radius": 6 * mm});
            skSolve(sketch);
        }
        {
            var Q0;
            Q0=makeQuery(id+"F16.imprint","IMPRINT",FACE,{"disambiguationData":[TD([[makeQuery(id+"F16.imprint","IMPRINT",EDGE,{"derivedFrom":sQuery(id+"F16.wireOp",EDGE,"E80")}),1.0]])]});
            var Q1;
            Q1=makeQuery(id+"F16.imprint","IMPRINT",FACE,{"disambiguationData":[TD([[makeQuery(id+"F16.imprint","IMPRINT",EDGE,{"derivedFrom":makeQuery(id+"F1.opExtrude","CAP_EDGE",EDGE,{"disambiguationData":[OSD([sQuery(id+"F0.wireOp",EDGE,"E1.left")])],"isStart":true})}),-1.0]])]});
            var Q2;
            Q2=makeQuery(id+"F16.imprint","IMPRINT",FACE,{"disambiguationData":[TD([[makeQuery(id+"F16.imprint","IMPRINT",EDGE,{"derivedFrom":sQuery(id+"F16.wireOp",EDGE,"E87.MirrorCS")}),1.0]])]});
            var Q3;
            Q3=makeQuery(id+"F2.opExtrude","CAP_FACE",FACE,{"disambiguationData":[OSD([sQuery(id+"F0.wireOp",EDGE,"E12"),sQuery(id+"F0.wireOp",EDGE,"E13"),sQuery(id+"F0.wireOp",EDGE,"E14"),sQuery(id+"F0.wireOp",EDGE,"E15"),sQuery(id+"F0.wireOp",EDGE,"E17.filletArc"),sQuery(id+"F0.wireOp",EDGE,"E18.filletArc"),sQuery(id+"F0.wireOp",EDGE,"E19.filletArc"),sQuery(id+"F0.wireOp",EDGE,"E20.filletArc"),sQuery(id+"F0.wireOp",EDGE,"E25.0"),sQuery(id+"F0.wireOp",EDGE,"E25.1"),sQuery(id+"F0.wireOp",EDGE,"E25.2"),sQuery(id+"F0.wireOp",EDGE,"E25.3"),sQuery(id+"F0.wireOp",EDGE,"E25.4"),sQuery(id+"F0.wireOp",EDGE,"E25.5"),sQuery(id+"F0.wireOp",EDGE,"E25.6"),sQuery(id+"F0.wireOp",EDGE,"E25.7")])],"isStart":false});
            extrude(context, id + "F17", {"entities" : qUnion([Q0, Q1, Q2]), "operationType" : NewBodyOperationType.ADD, "endBound" : BoundingType.UP_TO_SURFACE, "depth" : 25 * mm, "endBoundEntityFace" : qUnion([Q3]), "offsetDistance" : 25 * mm});
        }
    });
